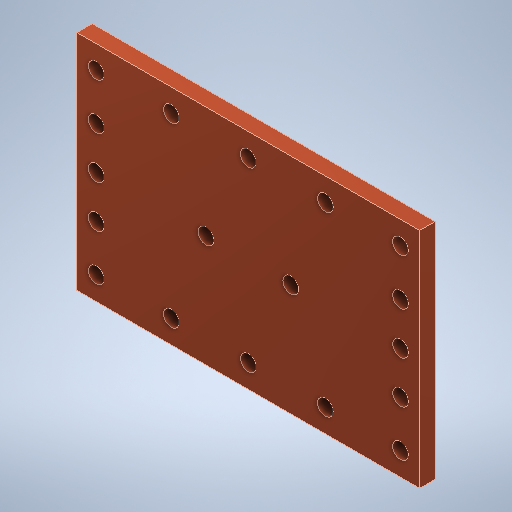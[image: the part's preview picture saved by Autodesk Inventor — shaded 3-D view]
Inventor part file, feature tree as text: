
AUTODESK INVENTOR PART (.ipt)
format: ipt  version: 2025.1 (Build 291241000, 241)  size: 281,088 bytes
history: native  units: mm
features: sketch x5, hole x4, extrude x1, plane x1, mirror x1
ambient origin geometry x8: Origin, YZ Plane, XZ Plane, XY Plane, X Axis, Y Axis, Z Axis, Center Point
bodies: Volumenkörper1 (feature_tree)
feature tree (12):
  extrude  "Extrusion1"  Depth=89.0mm
  hole  "Bohrung1"  [1 undecoded]
  plane  "Arbeitsebene1"
  mirror  "Spiegeln1"
  hole  "Bohrung2"  [1 undecoded]
  hole  "Bohrung3"  [1 undecoded]
  hole  "Hole4"  [1 undecoded]
  sketch  "Skizze1"  dims[d0=58.0mm d1=89.0mm]
  sketch  "Skizze2"  dims[d2=4.0mm d3=0.0mm d5=5.0mm]
  sketch  "Skizze3"  dims[d12=6.0mm d13=6.0mm]
  sketch  "Skizze4"  dims[d17=11.0mm d18=11.0mm]
  sketch  "Sketch9"  dims[d19=4.0mm d20=6.0mm d21=4.0mm d22=2.0mm d23=90.0deg d24=6.0mm d25=0.0mm d26=44.5mm d27=20.0mm d28=20.0mm d29=4.0mm d30=6.0mm d31=4.0mm d32=2.0mm d33=90.0deg d34=8.0mm d35=0.0mm d37=4.0mm d38=6.0mm d39=4.0mm d40=2.0mm d41=90.0deg d42=8.0mm d43=20.594885mm d44=6.0mm d45=6.0mm d67=22.0mm d68=11.0mm d69=4.0mm d70=6.0mm d71=4.0mm d72=2.0mm d73=90.0deg d74=8.0mm d75=0.0mm]
note: 4 required parameter values undecoded (feature->parameter linkage not recoverable at this tier; creation-order binding heuristic only, values carry confidence <= 0.55)
